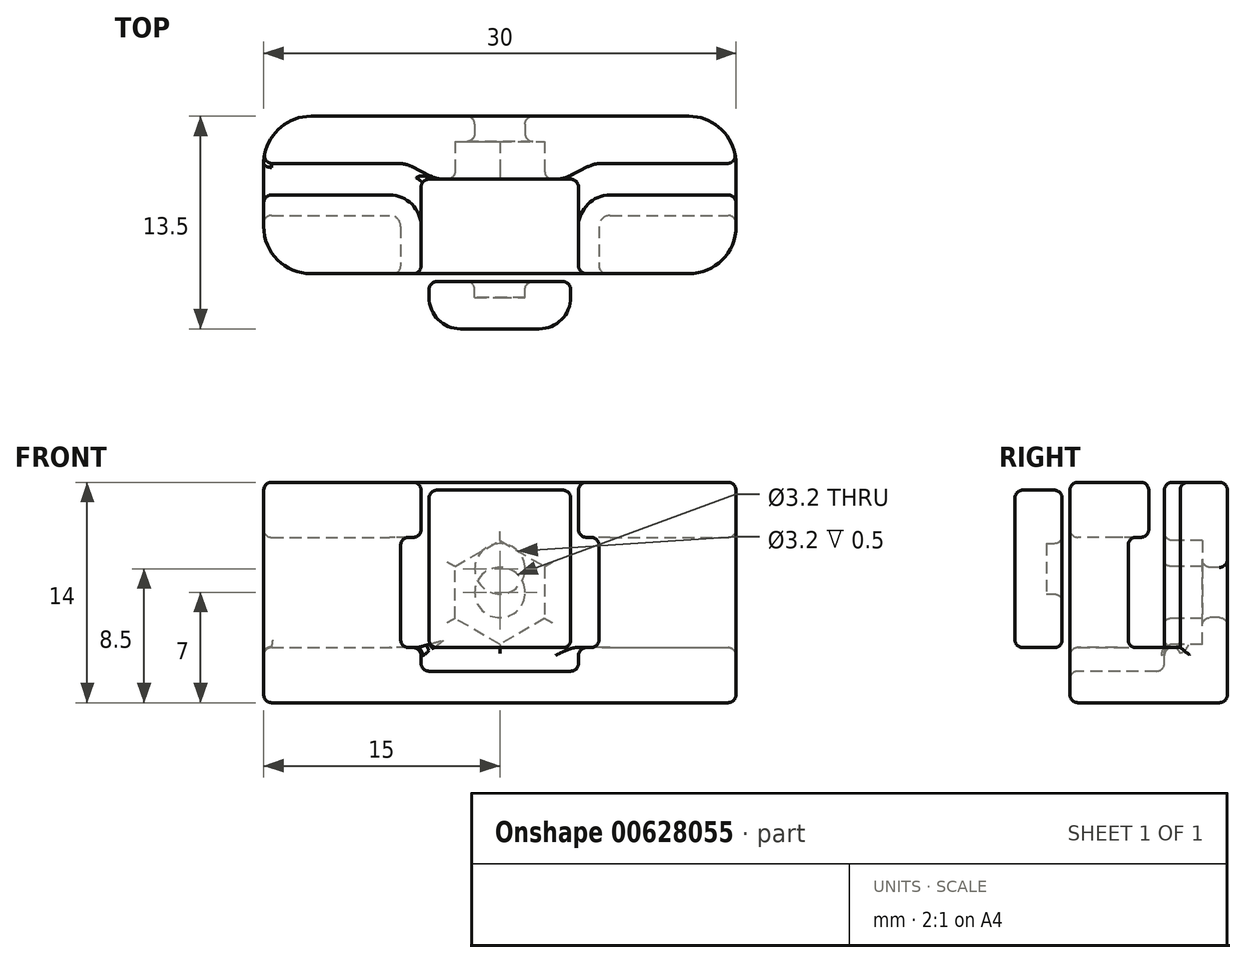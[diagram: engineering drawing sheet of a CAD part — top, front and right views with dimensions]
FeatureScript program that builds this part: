
annotation { "Feature Type Name" : "Feature", "Feature Type Description" : "" }
export const myFeature = defineFeature(function(context is Context, id is Id, definition is map)
    precondition{}
    {
        {
            var Q0;
            Q0=qCreatedBy(makeId("Top.planeOp"),FACE);
            var sketch = newSketch(context, id + "F0", { "sketchPlane" : qUnion([Q0])});
            skLineSegment(sketch, "E0", {"start": v(3, 0) * mm, "end": v(27, 0) * mm});
            skLineSegment(sketch, "E1", {"start": v(30, -3) * mm, "end": v(30, -7) * mm});
            skLineSegment(sketch, "E2", {"start": v(27, -10) * mm, "end": v(3, -10) * mm});
            skLineSegment(sketch, "E3", {"start": v(0, -7) * mm, "end": v(0, -3) * mm});
            skLineSegment(sketch, "E4", {"start": v(0, -5) * mm, "end": v(8, -5) * mm});
            skLineSegment(sketch, "E5", {"start": v(10, -7) * mm, "end": v(10, -10) * mm});
            skLineSegment(sketch, "E6", {"start": v(22, -5) * mm, "end": v(30, -5) * mm});
            skLineSegment(sketch, "E7", {"start": v(20, -7) * mm, "end": v(20, -10) * mm});
            skPoint(sketch, "E8.visualSharp", {"position": v(0, 0) * mm});
            skArc(sketch, "E8.filletArc", {"start": v(3, 0) * mm, "mid": v(0.88, -0.88) * mm, "end": v(0, -3) * mm});
            skPoint(sketch, "E9.visualSharp", {"position": v(30, 0) * mm});
            skArc(sketch, "E9.filletArc", {"start": v(30, -3) * mm, "mid": v(29.12, -0.88) * mm, "end": v(27, 0) * mm});
            skPoint(sketch, "E10.visualSharp", {"position": v(30, -10) * mm});
            skArc(sketch, "E10.filletArc", {"start": v(27, -10) * mm, "mid": v(29.12, -9.12) * mm, "end": v(30, -7) * mm});
            skPoint(sketch, "E11.visualSharp", {"position": v(0, -10) * mm});
            skArc(sketch, "E11.filletArc", {"start": v(0, -7) * mm, "mid": v(0.88, -9.12) * mm, "end": v(3, -10) * mm});
            skPoint(sketch, "E12.visualSharp", {"position": v(10, -5) * mm});
            skArc(sketch, "E12.filletArc", {"start": v(10, -7) * mm, "mid": v(9.41, -5.59) * mm, "end": v(8, -5) * mm});
            skPoint(sketch, "E13.visualSharp", {"position": v(20, -5) * mm});
            skArc(sketch, "E13.filletArc", {"start": v(22, -5) * mm, "mid": v(20.59, -5.59) * mm, "end": v(20, -7) * mm});
            skLineSegment(sketch, "E14", {"start": v(0, -3) * mm, "end": v(8.53, -3) * mm});
            skLineSegment(sketch, "E15", {"start": v(9, -3) * mm, "end": v(11, -3) * mm, "construction": true});
            skLineSegment(sketch, "E16", {"start": v(11, -3) * mm, "end": v(11, -4) * mm, "construction": true});
            skLineSegment(sketch, "E17", {"start": v(10.58, -3.79) * mm, "end": v(9.42, -3.21) * mm});
            skLineSegment(sketch, "E18", {"start": v(11.47, -4) * mm, "end": v(18.53, -4) * mm});
            skLineSegment(sketch, "E19", {"start": v(19, -4) * mm, "end": v(19, -3) * mm, "construction": true});
            skLineSegment(sketch, "E20", {"start": v(19, -3) * mm, "end": v(21, -3) * mm, "construction": true});
            skLineSegment(sketch, "E21", {"start": v(20.58, -3.21) * mm, "end": v(19.42, -3.79) * mm});
            skLineSegment(sketch, "E22", {"start": v(21.47, -3) * mm, "end": v(30, -3) * mm});
            skPoint(sketch, "E23.visualSharp", {"position": v(9, -3) * mm});
            skArc(sketch, "E23.filletArc", {"start": v(9.42, -3.21) * mm, "mid": v(8.99, -3.05) * mm, "end": v(8.53, -3) * mm});
            skPoint(sketch, "E24.visualSharp", {"position": v(11, -4) * mm});
            skArc(sketch, "E24.filletArc", {"start": v(10.58, -3.79) * mm, "mid": v(11.01, -3.95) * mm, "end": v(11.47, -4) * mm});
            skPoint(sketch, "E25.visualSharp", {"position": v(19, -4) * mm});
            skArc(sketch, "E25.filletArc", {"start": v(18.53, -4) * mm, "mid": v(18.99, -3.95) * mm, "end": v(19.42, -3.79) * mm});
            skPoint(sketch, "E26.visualSharp", {"position": v(21, -3) * mm});
            skArc(sketch, "E26.filletArc", {"start": v(21.47, -3) * mm, "mid": v(21.01, -3.05) * mm, "end": v(20.58, -3.21) * mm});
            skLineSegment(sketch, "E27.0", {"start": v(8.7, -7) * mm, "end": v(8.7, -10) * mm});
            skArc(sketch, "E27.1", {"start": v(8.7, -7) * mm, "mid": v(8.5, -6.5) * mm, "end": v(8, -6.3) * mm});
            skLineSegment(sketch, "E27.2", {"start": v(0, -6.3) * mm, "end": v(8, -6.3) * mm});
            skLineSegment(sketch, "E28.0", {"start": v(22, -6.3) * mm, "end": v(30, -6.3) * mm});
            skArc(sketch, "E28.1", {"start": v(22, -6.3) * mm, "mid": v(21.5, -6.5) * mm, "end": v(21.3, -7) * mm});
            skLineSegment(sketch, "E28.2", {"start": v(21.3, -7) * mm, "end": v(21.3, -10) * mm});
            skLineSegment(sketch, "E29", {"start": v(10.5, -10.5) * mm, "end": v(19.5, -10.5) * mm});
            skLineSegment(sketch, "E30", {"start": v(19.5, -10.5) * mm, "end": v(19.5, -11.5) * mm});
            skLineSegment(sketch, "E31", {"start": v(17.5, -13.5) * mm, "end": v(12.5, -13.5) * mm});
            skLineSegment(sketch, "E32", {"start": v(10.5, -11.5) * mm, "end": v(10.5, -10.5) * mm});
            skPoint(sketch, "E33.visualSharp", {"position": v(10.5, -13.5) * mm});
            skArc(sketch, "E33.filletArc", {"start": v(10.5, -11.5) * mm, "mid": v(11.09, -12.91) * mm, "end": v(12.5, -13.5) * mm});
            skPoint(sketch, "E34.visualSharp", {"position": v(19.5, -13.5) * mm});
            skArc(sketch, "E34.filletArc", {"start": v(17.5, -13.5) * mm, "mid": v(18.91, -12.91) * mm, "end": v(19.5, -11.5) * mm});
            skLineSegment(sketch, "E35", {"start": v(10, -7) * mm, "end": v(10, -4.5) * mm});
            skLineSegment(sketch, "E36", {"start": v(10.5, -4) * mm, "end": v(11.47, -4) * mm});
            skLineSegment(sketch, "E37", {"start": v(20, -7) * mm, "end": v(20, -4.5) * mm});
            skLineSegment(sketch, "E38", {"start": v(19.5, -4) * mm, "end": v(18.53, -4) * mm});
            skPoint(sketch, "E39.visualSharp", {"position": v(10, -4) * mm});
            skArc(sketch, "E39.filletArc", {"start": v(10.5, -4) * mm, "mid": v(10.15, -4.15) * mm, "end": v(10, -4.5) * mm});
            skPoint(sketch, "E40.visualSharp", {"position": v(20, -4) * mm});
            skArc(sketch, "E40.filletArc", {"start": v(20, -4.5) * mm, "mid": v(19.85, -4.15) * mm, "end": v(19.5, -4) * mm});
            skSolve(sketch);
        }
        {
            var Q0;
            Q0=makeQuery(id+"F0.imprint","IMPRINT",FACE,{"disambiguationData":[TD([[makeQuery(id+"F0.imprint","IMPRINT",EDGE,{"derivedFrom":sQuery(id+"F0.wireOp",EDGE,"E29")}),-1.0]])]});
            extrude(context, id + "F1", {"entities" : qUnion([Q0]), "depth" : 10 * mm, "offsetDistance" : 25 * mm});
        }
        {
            var Q0;
            Q0=makeQuery(id+"F0.imprint","IMPRINT",FACE,{"disambiguationData":[TD([[makeQuery(id+"F0.imprint","IMPRINT",EDGE,{"derivedFrom":sQuery(id+"F0.wireOp",EDGE,"E0")}),-1.0]])]});
            var Q1;
            {var subQ2=sQuery(id+"F0.wireOp",EDGE,"E4");Q1=makeQuery(id+"F0.imprint","IMPRINT",FACE,{"disambiguationData":[TD([[makeQuery(id+"F0.imprint","IMPRINT",EDGE,{"derivedFrom":subQ2}),1.0]])]});}
            var Q2;
            {var subQ0=sQuery(id+"F0.wireOp",EDGE,"E6");Q2=makeQuery(id+"F0.imprint","IMPRINT",FACE,{"disambiguationData":[TD([[makeQuery(id+"F0.imprint","IMPRINT",EDGE,{"derivedFrom":subQ0}),1.0]])]});}
            var Q3;
            {var subQ0=sQuery(id+"F0.wireOp",EDGE,"E10.filletArc");Q3=makeQuery(id+"F0.imprint","IMPRINT",FACE,{"disambiguationData":[TD([[makeQuery(id+"F0.imprint","IMPRINT",EDGE,{"derivedFrom":subQ0}),1.0]])]});}
            var Q4;
            {var subQ0=sQuery(id+"F0.wireOp",EDGE,"E6");Q4=makeQuery(id+"F0.imprint","IMPRINT",FACE,{"disambiguationData":[TD([[makeQuery(id+"F0.imprint","IMPRINT",EDGE,{"derivedFrom":subQ0}),-1.0]])]});}
            var Q5;
            {var subQ2=sQuery(id+"F0.wireOp",EDGE,"E4");Q5=makeQuery(id+"F0.imprint","IMPRINT",FACE,{"disambiguationData":[TD([[makeQuery(id+"F0.imprint","IMPRINT",EDGE,{"derivedFrom":subQ2}),-1.0]])]});}
            var Q6;
            {var subQ1=sQuery(id+"F0.wireOp",EDGE,"E11.filletArc");Q6=makeQuery(id+"F0.imprint","IMPRINT",FACE,{"disambiguationData":[TD([[makeQuery(id+"F0.imprint","IMPRINT",EDGE,{"derivedFrom":subQ1}),1.0]])]});}
            var Q7;
            {var subQ5=sQuery(id+"F0.wireOp",EDGE,"E5");Q7=makeQuery(id+"F0.imprint","IMPRINT",FACE,{"disambiguationData":[TD([[makeQuery(id+"F0.imprint","IMPRINT",EDGE,{"derivedFrom":subQ5}),1.0]])]});}
            extrude(context, id + "F2", {"entities" : qUnion([Q0, Q1, Q2, Q3, Q4, Q5, Q6, Q7]), "oppositeDirection" : true, "depth" : 3.5 * mm, "offsetDistance" : 25 * mm});
        }
        {
            var Q0;
            Q0=makeQuery(id+"F0.imprint","IMPRINT",FACE,{"disambiguationData":[TD([[makeQuery(id+"F0.imprint","IMPRINT",EDGE,{"derivedFrom":sQuery(id+"F0.wireOp",EDGE,"E0")}),-1.0]])]});
            var Q1;
            {var subQ2=sQuery(id+"F0.wireOp",EDGE,"E4");Q1=makeQuery(id+"F0.imprint","IMPRINT",FACE,{"disambiguationData":[TD([[makeQuery(id+"F0.imprint","IMPRINT",EDGE,{"derivedFrom":subQ2}),-1.0]])]});}
            var Q2;
            {var subQ1=sQuery(id+"F0.wireOp",EDGE,"E11.filletArc");Q2=makeQuery(id+"F0.imprint","IMPRINT",FACE,{"disambiguationData":[TD([[makeQuery(id+"F0.imprint","IMPRINT",EDGE,{"derivedFrom":subQ1}),1.0]])]});}
            var Q3;
            {var subQ0=sQuery(id+"F0.wireOp",EDGE,"E6");Q3=makeQuery(id+"F0.imprint","IMPRINT",FACE,{"disambiguationData":[TD([[makeQuery(id+"F0.imprint","IMPRINT",EDGE,{"derivedFrom":subQ0}),-1.0]])]});}
            var Q4;
            {var subQ0=sQuery(id+"F0.wireOp",EDGE,"E10.filletArc");Q4=makeQuery(id+"F0.imprint","IMPRINT",FACE,{"disambiguationData":[TD([[makeQuery(id+"F0.imprint","IMPRINT",EDGE,{"derivedFrom":subQ0}),1.0]])]});}
            extrude(context, id + "F3", {"entities" : qUnion([Q0, Q1, Q2, Q3, Q4]), "operationType" : NewBodyOperationType.ADD, "depth" : 10.5 * mm, "offsetDistance" : 25 * mm});
        }
        {
            var Q0;
            {var subQ2=sQuery(id+"F0.wireOp",EDGE,"E4");Q0=makeQuery(id+"F0.imprint","IMPRINT",FACE,{"disambiguationData":[TD([[makeQuery(id+"F0.imprint","IMPRINT",EDGE,{"derivedFrom":subQ2}),-1.0]])]});}
            var Q1;
            {var subQ0=sQuery(id+"F0.wireOp",EDGE,"E6");Q1=makeQuery(id+"F0.imprint","IMPRINT",FACE,{"disambiguationData":[TD([[makeQuery(id+"F0.imprint","IMPRINT",EDGE,{"derivedFrom":subQ0}),-1.0]])]});}
            extrude(context, id + "F4", {"entities" : qUnion([Q0, Q1]), "operationType" : NewBodyOperationType.REMOVE, "depth" : 7 * mm, "offsetDistance" : 25 * mm});
        }
        {
            var Q0;
            {var subQ5=sQuery(id+"F0.wireOp",EDGE,"E5");Q0=makeQuery(id+"F0.imprint","IMPRINT",FACE,{"disambiguationData":[TD([[makeQuery(id+"F0.imprint","IMPRINT",EDGE,{"derivedFrom":subQ5}),1.0]])]});}
            extrude(context, id + "F5", {"entities" : qUnion([Q0]), "operationType" : NewBodyOperationType.REMOVE, "oppositeDirection" : true, "depth" : 1.5 * mm, "offsetDistance" : 25 * mm});
        }
        {
            var Q0;
            {var subQ0=sQuery(id+"F0.wireOp",EDGE,"E18");Q0=makeQuery(id+"F5.boolean.opBoolean","MERGE",FACE,{"derivedFrom":[makeQuery(id+"F3.opExtrude","SWEPT_FACE",FACE,{"disambiguationData":[OSD([subQ0])]}),makeQuery(id+"F5.opExtrude","SWEPT_FACE",FACE,{"disambiguationData":[OSD([subQ0,sQuery(id+"F0.wireOp",EDGE,"E36"),sQuery(id+"F0.wireOp",EDGE,"E38")])]})]});}
            var sketch = newSketch(context, id + "F6", { "sketchPlane" : qUnion([Q0])});
            skCircle(sketch, "E41", {"center": v(15, 3.5) * mm, "radius": 1.6 * mm});
            skLineSegment(sketch, "E42", {"start": v(15, 3.5) * mm, "end": v(18.53, 3.5) * mm, "construction": true});
            skLineSegment(sketch, "E43", {"start": v(15, 3.5) * mm, "end": v(11.47, 3.5) * mm, "construction": true});
            skCircle(sketch, "E44.cCircle", {"center": v(15, 3.5) * mm, "radius": 2.85 * mm, "construction": true});
            skLineSegment(sketch, "E44.0", {"start": v(17.85, 5.15) * mm, "end": v(17.85, 1.85) * mm});
            skLineSegment(sketch, "E44.1", {"start": v(17.85, 1.85) * mm, "end": v(15, 0.2) * mm});
            skLineSegment(sketch, "E44.2", {"start": v(15, 0.2) * mm, "end": v(12.15, 1.85) * mm});
            skLineSegment(sketch, "E44.3", {"start": v(12.15, 1.85) * mm, "end": v(12.15, 5.15) * mm});
            skLineSegment(sketch, "E44.4", {"start": v(12.15, 5.15) * mm, "end": v(15, 6.8) * mm});
            skLineSegment(sketch, "E44.5", {"start": v(15, 6.8) * mm, "end": v(17.85, 5.15) * mm});
            skPoint(sketch, "E44.0.midPoint", {"position": v(17.85, 3.5) * mm});
            skSolve(sketch);
        }
        {
            var Q0;
            Q0=makeQuery(id+"F6.imprint","IMPRINT",FACE,{"disambiguationData":[TD([[makeQuery(id+"F6.imprint","IMPRINT",EDGE,{"derivedFrom":sQuery(id+"F6.wireOp",EDGE,"E41")}),1.0]])]});
            extrude(context, id + "F7", {"entities" : qUnion([Q0]), "operationType" : NewBodyOperationType.REMOVE, "oppositeDirection" : true, "depth" : 4 * mm, "offsetDistance" : 25 * mm});
        }
        {
            var Q0;
            Q0=makeQuery(id+"F6.imprint","IMPRINT",FACE,{"disambiguationData":[TD([[makeQuery(id+"F6.imprint","IMPRINT",EDGE,{"derivedFrom":sQuery(id+"F6.wireOp",EDGE,"E41")}),-1.0]])]});
            extrude(context, id + "F8", {"entities" : qUnion([Q0]), "operationType" : NewBodyOperationType.REMOVE, "oppositeDirection" : true, "depth" : 2.4 * mm, "offsetDistance" : 25 * mm});
        }
        {
            var Q0;
            Q0=makeQuery(id+"F1.opExtrude","SWEPT_FACE",FACE,{"disambiguationData":[OSD([sQuery(id+"F0.wireOp",EDGE,"E29")])]});
            var sketch = newSketch(context, id + "F9", { "sketchPlane" : qUnion([Q0])});
            skCircle(sketch, "E45", {"center": v(-15, 5) * mm, "radius": 1.6 * mm});
            skSolve(sketch);
        }
        {
            var Q0;
            Q0=makeQuery(id+"F9.imprint","IMPRINT",FACE,{"disambiguationData":[TD([[makeQuery(id+"F9.imprint","IMPRINT",EDGE,{"derivedFrom":sQuery(id+"F9.wireOp",EDGE,"E45")}),1.0]])]});
            extrude(context, id + "F10", {"entities" : qUnion([Q0]), "operationType" : NewBodyOperationType.REMOVE, "oppositeDirection" : true, "depth" : 1 * mm, "offsetDistance" : 25 * mm});
        }
        {
            var Q0;
            Q0=makeQuery(id+"F3.opExtrude","CAP_EDGE",EDGE,{"disambiguationData":[OSD([sQuery(id+"F0.wireOp",EDGE,"E0")])],"isStart":false});
            var Q1;
            Q1=makeQuery(id+"F7.boolean.opBoolean","COPY",FACE,{"derivedFrom":makeQuery(id+"F7.opExtrude","SWEPT_FACE",FACE,{"disambiguationData":[OSD([sQuery(id+"F6.wireOp",EDGE,"E41")])]})});
            var Q2;
            Q2=makeQuery(id+"F2.opExtrude","CAP_EDGE",EDGE,{"disambiguationData":[OSD([sQuery(id+"F0.wireOp",EDGE,"E0")])],"isStart":false});
            var Q3;
            Q3=makeQuery(id+"F3.opExtrude","CAP_EDGE",EDGE,{"disambiguationData":[OSD([sQuery(id+"F0.wireOp",EDGE,"E22")])],"isStart":false});
            var Q4;
            Q4=makeQuery(id+"F3.opExtrude","SWEPT_EDGE",EDGE,{"disambiguationData":[OSD([sQuery(id+"F0.wireOp",EDGE,"E3"),sQuery(id+"F0.wireOp",EDGE,"E8.filletArc"),sQuery(id+"F0.wireOp",EDGE,"E14")])]});
            var Q5;
            {var subQ0=sQuery(id+"F0.wireOp",EDGE,"E3");Q5=makeQuery(id+"F4.boolean.opBoolean","MERGE",EDGE,{"derivedFrom":[makeQuery(id+"F2.opExtrude","CAP_EDGE",EDGE,{"disambiguationData":[OSD([subQ0])],"isStart":true}),makeQuery(id+"F4.opExtrude","CAP_EDGE",EDGE,{"disambiguationData":[OSD([subQ0])],"isStart":true})]});}
            var Q6;
            Q6=makeQuery(id+"F4.boolean.opBoolean","COPY",EDGE,{"derivedFrom":makeQuery(id+"F4.opExtrude","SWEPT_EDGE",EDGE,{"disambiguationData":[OSD([sQuery(id+"F0.wireOp",EDGE,"E3"),sQuery(id+"F0.wireOp",EDGE,"E27.2")])]})});
            var Q7;
            Q7=makeQuery(id+"F3.opExtrude","CAP_FACE",FACE,{"disambiguationData":[OSD([sQuery(id+"F0.wireOp",EDGE,"E2"),sQuery(id+"F0.wireOp",EDGE,"E3"),sQuery(id+"F0.wireOp",EDGE,"E4"),sQuery(id+"F0.wireOp",EDGE,"E5"),sQuery(id+"F0.wireOp",EDGE,"E11.filletArc"),sQuery(id+"F0.wireOp",EDGE,"E12.filletArc")])],"isStart":false});
            var Q8;
            Q8=makeQuery(id+"F3.opExtrude","CAP_FACE",FACE,{"disambiguationData":[OSD([sQuery(id+"F0.wireOp",EDGE,"E1"),sQuery(id+"F0.wireOp",EDGE,"E2"),sQuery(id+"F0.wireOp",EDGE,"E6"),sQuery(id+"F0.wireOp",EDGE,"E7"),sQuery(id+"F0.wireOp",EDGE,"E10.filletArc"),sQuery(id+"F0.wireOp",EDGE,"E13.filletArc")])],"isStart":false});
            var Q9;
            Q9=makeQuery(id+"F1.opExtrude","CAP_FACE",FACE,{"disambiguationData":[OSD([sQuery(id+"F0.wireOp",EDGE,"E29"),sQuery(id+"F0.wireOp",EDGE,"E30"),sQuery(id+"F0.wireOp",EDGE,"E31"),sQuery(id+"F0.wireOp",EDGE,"E32"),sQuery(id+"F0.wireOp",EDGE,"E33.filletArc"),sQuery(id+"F0.wireOp",EDGE,"E34.filletArc")])],"isStart":false});
            var Q10;
            Q10=makeQuery(id+"F1.opExtrude","CAP_FACE",FACE,{"disambiguationData":[OSD([sQuery(id+"F0.wireOp",EDGE,"E29"),sQuery(id+"F0.wireOp",EDGE,"E30"),sQuery(id+"F0.wireOp",EDGE,"E31"),sQuery(id+"F0.wireOp",EDGE,"E32"),sQuery(id+"F0.wireOp",EDGE,"E33.filletArc"),sQuery(id+"F0.wireOp",EDGE,"E34.filletArc")])],"isStart":true});
            var Q11;
            Q11=makeQuery(id+"F1.opExtrude","SWEPT_FACE",FACE,{"disambiguationData":[OSD([sQuery(id+"F0.wireOp",EDGE,"E29")])]});
            var Q12;
            {var subQ0=sQuery(id+"F0.wireOp",EDGE,"E3");Q12=makeQuery(id+"F3.boolean.opBoolean","MERGE",FACE,{"derivedFrom":[makeQuery(id+"F2.opExtrude","SWEPT_FACE",FACE,{"disambiguationData":[OSD([subQ0])]}),makeQuery(id+"F3.opExtrude","SWEPT_FACE",FACE,{"disambiguationData":[OSD([subQ0])]})]});}
            var Q13;
            {var subQ0=sQuery(id+"F0.wireOp",EDGE,"E2");Q13=makeQuery(id+"F3.boolean.opBoolean","MERGE",FACE,{"derivedFrom":[makeQuery(id+"F2.opExtrude","SWEPT_FACE",FACE,{"disambiguationData":[OSD([subQ0])]}),makeQuery(id+"F3.opExtrude","SWEPT_FACE",FACE,{"disambiguationData":[OSD([subQ0]),TDD([makeQuery(id+"F0.imprint","IMPRINT",EDGE,{"disambiguationData":[TD([[makeQuery(id+"F0.imprint","INTERSECT",VERTEX,{"derivedFrom":[subQ0,sQuery(id+"F0.wireOp",EDGE,"E10.filletArc")]}),-1.0]])],"derivedFrom":subQ0}),makeQuery(id+"F0.imprint","IMPRINT",EDGE,{"disambiguationData":[TD([[makeQuery(id+"F0.imprint","INTERSECT",VERTEX,{"derivedFrom":[subQ0,sQuery(id+"F0.wireOp",EDGE,"E7")]}),1.0]])],"derivedFrom":subQ0})])]}),makeQuery(id+"F3.opExtrude","SWEPT_FACE",FACE,{"disambiguationData":[OSD([subQ0]),TDD([makeQuery(id+"F0.imprint","IMPRINT",EDGE,{"disambiguationData":[TD([[makeQuery(id+"F0.imprint","INTERSECT",VERTEX,{"derivedFrom":[subQ0,sQuery(id+"F0.wireOp",EDGE,"E5")]}),-1.0]])],"derivedFrom":subQ0}),makeQuery(id+"F0.imprint","IMPRINT",EDGE,{"disambiguationData":[TD([[makeQuery(id+"F0.imprint","INTERSECT",VERTEX,{"derivedFrom":[subQ0,sQuery(id+"F0.wireOp",EDGE,"E11.filletArc")]}),1.0]])],"derivedFrom":subQ0})])]})]});}
            var Q14;
            Q14=makeQuery(id+"F4.boolean.opBoolean","COPY",FACE,{"derivedFrom":makeQuery(id+"F4.opExtrude","CAP_FACE",FACE,{"disambiguationData":[OSD([sQuery(id+"F0.wireOp",EDGE,"E2"),sQuery(id+"F0.wireOp",EDGE,"E3"),sQuery(id+"F0.wireOp",EDGE,"E4"),sQuery(id+"F0.wireOp",EDGE,"E5"),sQuery(id+"F0.wireOp",EDGE,"E12.filletArc"),sQuery(id+"F0.wireOp",EDGE,"E27.0"),sQuery(id+"F0.wireOp",EDGE,"E27.1"),sQuery(id+"F0.wireOp",EDGE,"E27.2")])],"isStart":false})});
            var Q15;
            {var subQ0=sQuery(id+"F0.wireOp",EDGE,"E8.filletArc");var subQ1=sQuery(id+"F0.wireOp",EDGE,"E3");var subQ2=sQuery(id+"F0.wireOp",EDGE,"E11.filletArc");var subQ3=sQuery(id+"F0.wireOp",EDGE,"E2");var subQ4=sQuery(id+"F0.wireOp",EDGE,"E27.0");var subQ6=sQuery(id+"F0.wireOp",EDGE,"E5");var subQ8=sQuery(id+"F0.wireOp",EDGE,"E7");var subQ9=sQuery(id+"F0.wireOp",EDGE,"E28.2");var subQ11=sQuery(id+"F0.wireOp",EDGE,"E10.filletArc");var subQ12=sQuery(id+"F0.wireOp",EDGE,"E27.1");var subQ13=sQuery(id+"F0.wireOp",EDGE,"E27.2");var subQ14=sQuery(id+"F0.wireOp",EDGE,"E1");Q15=makeQuery(id+"F5.boolean.opBoolean","SPLIT",FACE,{"disambiguationData":[TD([makeQuery(id+"F2.opExtrude","SWEPT_FACE",FACE,{"disambiguationData":[OSD([subQ1])]})])],"derivedFrom":makeQuery(id+"F4.boolean.opBoolean","MERGE",FACE,{"derivedFrom":[makeQuery(id+"F2.opExtrude","CAP_FACE",FACE,{"disambiguationData":[OSD([sQuery(id+"F0.wireOp",EDGE,"E0"),subQ14,subQ3,subQ1,subQ0,sQuery(id+"F0.wireOp",EDGE,"E9.filletArc"),subQ11,subQ2])],"isStart":true}),makeQuery(id+"F4.opExtrude","CAP_FACE",FACE,{"disambiguationData":[OSD([subQ14,subQ3,sQuery(id+"F0.wireOp",EDGE,"E6"),subQ8,sQuery(id+"F0.wireOp",EDGE,"E13.filletArc"),sQuery(id+"F0.wireOp",EDGE,"E28.0"),sQuery(id+"F0.wireOp",EDGE,"E28.1"),subQ9])],"isStart":true}),makeQuery(id+"F4.opExtrude","CAP_FACE",FACE,{"disambiguationData":[OSD([subQ3,subQ1,sQuery(id+"F0.wireOp",EDGE,"E4"),subQ6,sQuery(id+"F0.wireOp",EDGE,"E12.filletArc"),subQ4,subQ12,subQ13])],"isStart":true})]})});}
            var Q16;
            {var subQ0=sQuery(id+"F0.wireOp",EDGE,"E10.filletArc");Q16=makeQuery(id+"F3.boolean.opBoolean","MERGE",FACE,{"derivedFrom":[makeQuery(id+"F2.opExtrude","SWEPT_FACE",FACE,{"disambiguationData":[OSD([subQ0])]}),makeQuery(id+"F3.opExtrude","SWEPT_FACE",FACE,{"disambiguationData":[OSD([subQ0])]})]});}
            var Q17;
            {var subQ0=sQuery(id+"F0.wireOp",EDGE,"E1");Q17=makeQuery(id+"F3.boolean.opBoolean","MERGE",FACE,{"derivedFrom":[makeQuery(id+"F2.opExtrude","SWEPT_FACE",FACE,{"disambiguationData":[OSD([subQ0])]}),makeQuery(id+"F3.opExtrude","SWEPT_FACE",FACE,{"disambiguationData":[OSD([subQ0])]})]});}
            var Q18;
            Q18=makeQuery(id+"F4.boolean.opBoolean","COPY",FACE,{"derivedFrom":makeQuery(id+"F4.opExtrude","SWEPT_FACE",FACE,{"disambiguationData":[OSD([sQuery(id+"F0.wireOp",EDGE,"E28.0")])]})});
            var Q19;
            Q19=makeQuery(id+"F3.opExtrude","SWEPT_FACE",FACE,{"disambiguationData":[OSD([sQuery(id+"F0.wireOp",EDGE,"E6")])]});
            var Q20;
            {var subQ0=sQuery(id+"F0.wireOp",EDGE,"E9.filletArc");Q20=makeQuery(id+"F3.boolean.opBoolean","MERGE",FACE,{"derivedFrom":[makeQuery(id+"F2.opExtrude","SWEPT_FACE",FACE,{"disambiguationData":[OSD([subQ0])]}),makeQuery(id+"F3.opExtrude","SWEPT_FACE",FACE,{"disambiguationData":[OSD([subQ0])]})]});}
            var Q21;
            Q21=makeQuery(id+"F5.boolean.opBoolean","COPY",FACE,{"derivedFrom":makeQuery(id+"F5.opExtrude","CAP_FACE",FACE,{"disambiguationData":[OSD([sQuery(id+"F0.wireOp",EDGE,"E2"),sQuery(id+"F0.wireOp",EDGE,"E5"),sQuery(id+"F0.wireOp",EDGE,"E7"),sQuery(id+"F0.wireOp",EDGE,"E18"),sQuery(id+"F0.wireOp",EDGE,"E35"),sQuery(id+"F0.wireOp",EDGE,"E36"),sQuery(id+"F0.wireOp",EDGE,"E37"),sQuery(id+"F0.wireOp",EDGE,"E38"),sQuery(id+"F0.wireOp",EDGE,"E39.filletArc"),sQuery(id+"F0.wireOp",EDGE,"E40.filletArc")])],"isStart":false})});
            var Q22;
            Q22=makeQuery(id+"F5.boolean.opBoolean","COPY",EDGE,{"derivedFrom":makeQuery(id+"F5.opExtrude","CAP_EDGE",EDGE,{"disambiguationData":[OSD([sQuery(id+"F0.wireOp",EDGE,"E7"),sQuery(id+"F0.wireOp",EDGE,"E37")])],"isStart":true})});
            var Q23;
            {var subQ0=sQuery(id+"F0.wireOp",EDGE,"E18");Q23=makeQuery(id+"F5.boolean.opBoolean","MERGE",FACE,{"derivedFrom":[makeQuery(id+"F3.opExtrude","SWEPT_FACE",FACE,{"disambiguationData":[OSD([subQ0])]}),makeQuery(id+"F5.opExtrude","SWEPT_FACE",FACE,{"disambiguationData":[OSD([subQ0,sQuery(id+"F0.wireOp",EDGE,"E36"),sQuery(id+"F0.wireOp",EDGE,"E38")])]})]});}
            var Q24;
            Q24=makeQuery(id+"F3.opExtrude","CAP_EDGE",EDGE,{"disambiguationData":[OSD([sQuery(id+"F0.wireOp",EDGE,"E22")])],"isStart":true});
            fillet(context, id + "F11", {"entities" : qUnion([Q0, Q1, Q2, Q3, Q4, Q5, Q6, Q7, Q8, Q9, Q10, Q11, Q12, Q13, Q14, Q15, Q16, Q17, Q18, Q19, Q20, Q21, Q22, Q23, Q24]), "radius" : 0.5 * mm, "tangentPropagation" : true, "allowEdgeOverflow" : false});
        }
    });
